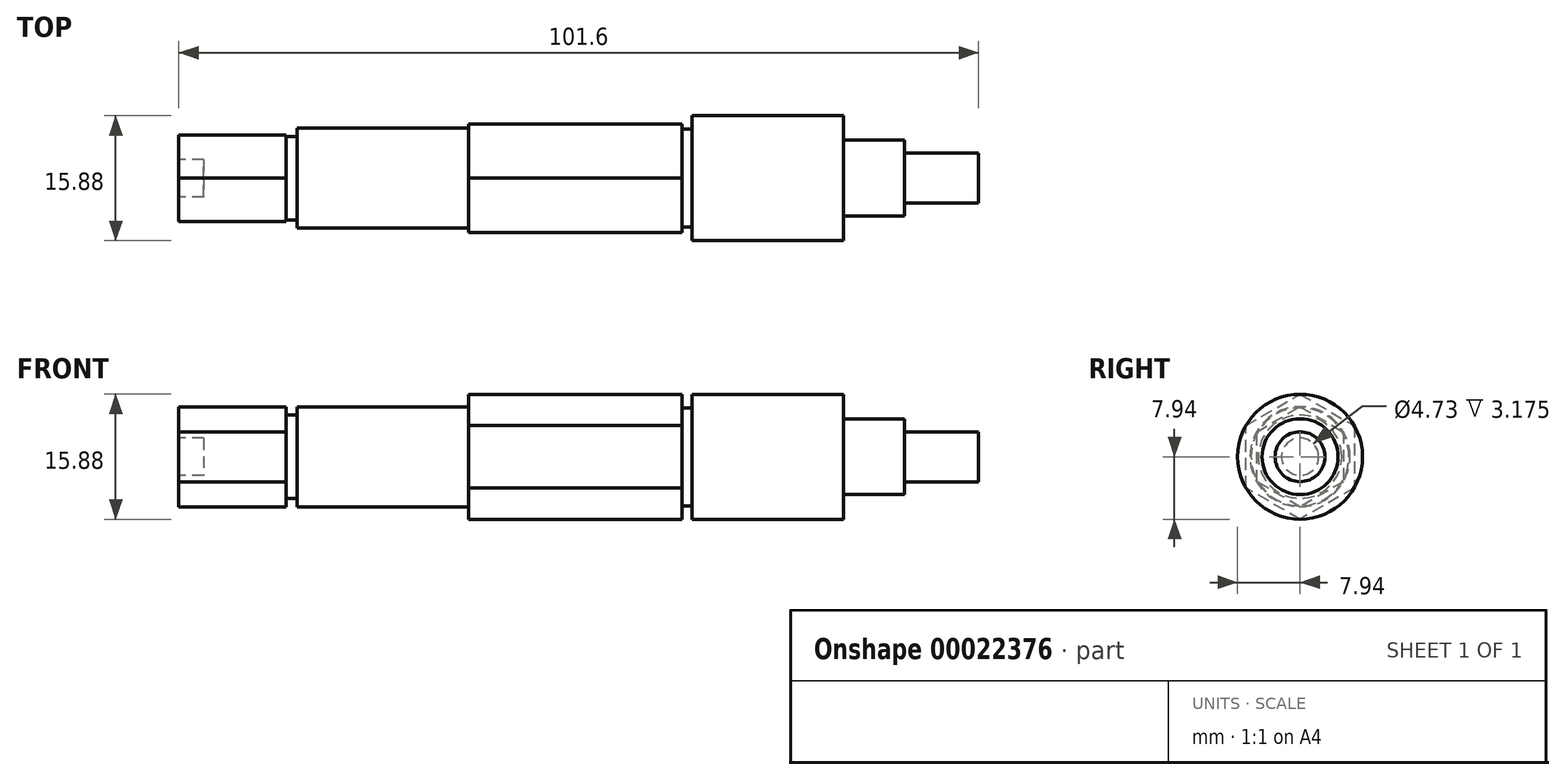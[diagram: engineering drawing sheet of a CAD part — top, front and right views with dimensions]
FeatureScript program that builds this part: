
annotation { "Feature Type Name" : "Feature", "Feature Type Description" : "" }
export const myFeature = defineFeature(function(context is Context, id is Id, definition is map)
    precondition{}
    {
        {
            var Q0;
            Q0=qCreatedBy(makeId("Front.planeOp"),FACE);
            var sketch = newSketch(context, id + "F0", { "sketchPlane" : qUnion([Q0])});
            skLineSegment(sketch, "E0", {"start": v(0, 0) * mm, "end": v(101.6, 0) * mm});
            skLineSegment(sketch, "E1", {"start": v(101.6, 0) * mm, "end": v(101.6, 3.17) * mm});
            skLineSegment(sketch, "E2", {"start": v(101.6, 3.17) * mm, "end": v(92.2, 3.17) * mm});
            skLineSegment(sketch, "E3", {"start": v(92.2, 3.17) * mm, "end": v(92.2, 4.83) * mm});
            skLineSegment(sketch, "E4", {"start": v(92.2, 4.83) * mm, "end": v(84.43, 4.83) * mm});
            skLineSegment(sketch, "E5", {"start": v(84.43, 4.83) * mm, "end": v(84.43, 7.94) * mm});
            skLineSegment(sketch, "E6", {"start": v(84.43, 7.94) * mm, "end": v(65.2, 7.94) * mm});
            skLineSegment(sketch, "E7", {"start": v(36.79, 7.94) * mm, "end": v(36.79, 6.35) * mm});
            skLineSegment(sketch, "E8", {"start": v(36.79, 6.35) * mm, "end": v(15.02, 6.35) * mm});
            skLineSegment(sketch, "E9", {"start": v(0, 6.35) * mm, "end": v(0, 0) * mm});
            skLineSegment(sketch, "E10.top", {"start": v(63.94, 6.22) * mm, "end": v(65.2, 6.22) * mm});
            skLineSegment(sketch, "E10.left", {"start": v(63.94, 7.94) * mm, "end": v(63.94, 6.22) * mm});
            skLineSegment(sketch, "E10.right", {"start": v(65.2, 7.94) * mm, "end": v(65.2, 6.22) * mm});
            skLineSegment(sketch, "E11.top", {"start": v(13.61, 5.3) * mm, "end": v(15.02, 5.3) * mm});
            skLineSegment(sketch, "E11.left", {"start": v(13.61, 6.35) * mm, "end": v(13.61, 5.3) * mm});
            skLineSegment(sketch, "E11.right", {"start": v(15.02, 6.35) * mm, "end": v(15.02, 5.3) * mm});
            skLineSegment(sketch, "E12.trimOffspring", {"start": v(13.61, 6.35) * mm, "end": v(0, 6.35) * mm});
            skLineSegment(sketch, "E13.trimOffspring", {"start": v(63.94, 7.94) * mm, "end": v(36.79, 7.94) * mm});
            skLineSegment(sketch, "E14", {"start": v(101.6, 0) * mm, "end": v(124.76, 0) * mm, "construction": true});
            skLineSegment(sketch, "E15", {"start": v(0, 6.35) * mm, "end": v(0, 23.71) * mm, "construction": true});
            skSolve(sketch);
        }
        {
            var Q0;
            Q0=makeQuery(id+"F0.imprint","IMPRINT",FACE,{"disambiguationData":[TD([[makeQuery(id+"F0.imprint","IMPRINT",EDGE,{"derivedFrom":sQuery(id+"F0.wireOp",EDGE,"E0")}),1.0]])]});
            var Q1;
            Q1=sQuery(id+"F0.wireOp",EDGE,"E0");
            revolve(context, id + "F1", {"entities" : qUnion([Q0]), "axis" : qUnion([Q1]), "revolveType" : RevolveType.FULL, "oppositeDirection" : true});
        }
        {
            var Q0;
            Q0=makeQuery(id+"F1.opRevolve","SWEPT_FACE",FACE,{"disambiguationData":[OSD([sQuery(id+"F0.wireOp",EDGE,"E9")])]});
            var sketch = newSketch(context, id + "F2", { "sketchPlane" : qUnion([Q0])});
            skCircle(sketch, "E16", {"center": v(0, 0) * mm, "radius": 2.36 * mm});
            skSolve(sketch);
        }
        {
            var Q0;
            Q0=makeQuery(id+"F2.imprint","IMPRINT",FACE,{"disambiguationData":[TD([[makeQuery(id+"F2.imprint","IMPRINT",EDGE,{"derivedFrom":sQuery(id+"F2.wireOp",EDGE,"E16")}),1.0]])]});
            extrude(context, id + "F3", {"entities" : qUnion([Q0]), "operationType" : NewBodyOperationType.REMOVE, "oppositeDirection" : true, "depth" : 3.17 * mm});
        }
        {
            var Q0;
            Q0=makeQuery(id+"F1.opRevolve","SWEPT_FACE",FACE,{"disambiguationData":[OSD([sQuery(id+"F0.wireOp",EDGE,"E9")])]});
            var sketch = newSketch(context, id + "F4", { "sketchPlane" : qUnion([Q0])});
            skCircle(sketch, "E17.cCircle", {"center": v(0, 0) * mm, "radius": 6.35 * mm, "construction": true});
            skLineSegment(sketch, "E17.0", {"start": v(0, 6.35) * mm, "end": v(5.5, 3.17) * mm});
            skLineSegment(sketch, "E17.1", {"start": v(5.5, 3.17) * mm, "end": v(5.5, -3.17) * mm});
            skLineSegment(sketch, "E17.2", {"start": v(5.5, -3.17) * mm, "end": v(0, -6.35) * mm});
            skLineSegment(sketch, "E17.3", {"start": v(0, -6.35) * mm, "end": v(-5.5, -3.17) * mm});
            skLineSegment(sketch, "E17.4", {"start": v(-5.5, -3.17) * mm, "end": v(-5.5, 3.17) * mm});
            skLineSegment(sketch, "E17.5", {"start": v(-5.5, 3.17) * mm, "end": v(0, 6.35) * mm});
            skSolve(sketch);
        }
        {
            var Q0;
            {var subQ1=sQuery(id+"F4.wireOp",EDGE,"E17.0");Q0=makeQuery(id+"F4.imprint","IMPRINT",FACE,{"disambiguationData":[TD([[makeQuery(id+"F4.imprint","IMPRINT",EDGE,{"derivedFrom":subQ1}),1.0]])]});}
            var Q1;
            {var subQ1=sQuery(id+"F4.wireOp",EDGE,"E17.1");Q1=makeQuery(id+"F4.imprint","IMPRINT",FACE,{"disambiguationData":[TD([[makeQuery(id+"F4.imprint","IMPRINT",EDGE,{"derivedFrom":subQ1}),1.0]])]});}
            var Q2;
            {var subQ1=sQuery(id+"F4.wireOp",EDGE,"E17.2");Q2=makeQuery(id+"F4.imprint","IMPRINT",FACE,{"disambiguationData":[TD([[makeQuery(id+"F4.imprint","IMPRINT",EDGE,{"derivedFrom":subQ1}),1.0]])]});}
            var Q3;
            {var subQ1=sQuery(id+"F4.wireOp",EDGE,"E17.3");Q3=makeQuery(id+"F4.imprint","IMPRINT",FACE,{"disambiguationData":[TD([[makeQuery(id+"F4.imprint","IMPRINT",EDGE,{"derivedFrom":subQ1}),1.0]])]});}
            var Q4;
            {var subQ1=sQuery(id+"F4.wireOp",EDGE,"E17.4");Q4=makeQuery(id+"F4.imprint","IMPRINT",FACE,{"disambiguationData":[TD([[makeQuery(id+"F4.imprint","IMPRINT",EDGE,{"derivedFrom":subQ1}),1.0]])]});}
            var Q5;
            {var subQ1=sQuery(id+"F4.wireOp",EDGE,"E17.5");Q5=makeQuery(id+"F4.imprint","IMPRINT",FACE,{"disambiguationData":[TD([[makeQuery(id+"F4.imprint","IMPRINT",EDGE,{"derivedFrom":subQ1}),1.0]])]});}
            var Q6;
            Q6=makeQuery(id+"F1.opRevolve","SWEPT_FACE",FACE,{"disambiguationData":[OSD([sQuery(id+"F0.wireOp",EDGE,"E11.left")])]});
            extrude(context, id + "F5", {"entities" : qUnion([Q0, Q1, Q2, Q3, Q4, Q5]), "operationType" : NewBodyOperationType.REMOVE, "endBound" : BoundingType.UP_TO_SURFACE, "oppositeDirection" : true, "endBoundEntityFace" : qUnion([Q6]), "depth" : 10.8 * mm});
        }
        {
            var Q0;
            Q0=makeQuery(id+"F1.opRevolve","SWEPT_FACE",FACE,{"disambiguationData":[OSD([sQuery(id+"F0.wireOp",EDGE,"E7")])]});
            var sketch = newSketch(context, id + "F6", { "sketchPlane" : qUnion([Q0])});
            skCircle(sketch, "E18.cCircle", {"center": v(0, 0) * mm, "radius": 7.94 * mm, "construction": true});
            skLineSegment(sketch, "E18.0", {"start": v(0, 7.94) * mm, "end": v(6.87, 3.97) * mm});
            skLineSegment(sketch, "E18.1", {"start": v(6.87, 3.97) * mm, "end": v(6.87, -3.97) * mm});
            skLineSegment(sketch, "E18.2", {"start": v(6.87, -3.97) * mm, "end": v(0, -7.94) * mm});
            skLineSegment(sketch, "E18.3", {"start": v(0, -7.94) * mm, "end": v(-6.87, -3.97) * mm});
            skLineSegment(sketch, "E18.4", {"start": v(-6.87, -3.97) * mm, "end": v(-6.87, 3.97) * mm});
            skLineSegment(sketch, "E18.5", {"start": v(-6.87, 3.97) * mm, "end": v(0, 7.94) * mm});
            skSolve(sketch);
        }
        {
            var Q0;
            {var subQ1=sQuery(id+"F6.wireOp",EDGE,"E18.0");Q0=makeQuery(id+"F6.imprint","IMPRINT",FACE,{"disambiguationData":[TD([[makeQuery(id+"F6.imprint","IMPRINT",EDGE,{"derivedFrom":subQ1}),1.0]])]});}
            var Q1;
            {var subQ1=sQuery(id+"F6.wireOp",EDGE,"E18.1");Q1=makeQuery(id+"F6.imprint","IMPRINT",FACE,{"disambiguationData":[TD([[makeQuery(id+"F6.imprint","IMPRINT",EDGE,{"derivedFrom":subQ1}),1.0]])]});}
            var Q2;
            {var subQ1=sQuery(id+"F6.wireOp",EDGE,"E18.5");Q2=makeQuery(id+"F6.imprint","IMPRINT",FACE,{"disambiguationData":[TD([[makeQuery(id+"F6.imprint","IMPRINT",EDGE,{"derivedFrom":subQ1}),1.0]])]});}
            var Q3;
            {var subQ1=sQuery(id+"F6.wireOp",EDGE,"E18.4");Q3=makeQuery(id+"F6.imprint","IMPRINT",FACE,{"disambiguationData":[TD([[makeQuery(id+"F6.imprint","IMPRINT",EDGE,{"derivedFrom":subQ1}),1.0]])]});}
            var Q4;
            {var subQ1=sQuery(id+"F6.wireOp",EDGE,"E18.3");Q4=makeQuery(id+"F6.imprint","IMPRINT",FACE,{"disambiguationData":[TD([[makeQuery(id+"F6.imprint","IMPRINT",EDGE,{"derivedFrom":subQ1}),1.0]])]});}
            var Q5;
            {var subQ1=sQuery(id+"F6.wireOp",EDGE,"E18.2");Q5=makeQuery(id+"F6.imprint","IMPRINT",FACE,{"disambiguationData":[TD([[makeQuery(id+"F6.imprint","IMPRINT",EDGE,{"derivedFrom":subQ1}),1.0]])]});}
            var Q6;
            Q6=makeQuery(id+"F1.opRevolve","SWEPT_FACE",FACE,{"disambiguationData":[OSD([sQuery(id+"F0.wireOp",EDGE,"E10.left")])]});
            extrude(context, id + "F7", {"entities" : qUnion([Q0, Q1, Q2, Q3, Q4, Q5]), "operationType" : NewBodyOperationType.REMOVE, "endBound" : BoundingType.UP_TO_SURFACE, "oppositeDirection" : true, "endBoundEntityFace" : qUnion([Q6]), "depth" : 17.9 * mm});
        }
    });
